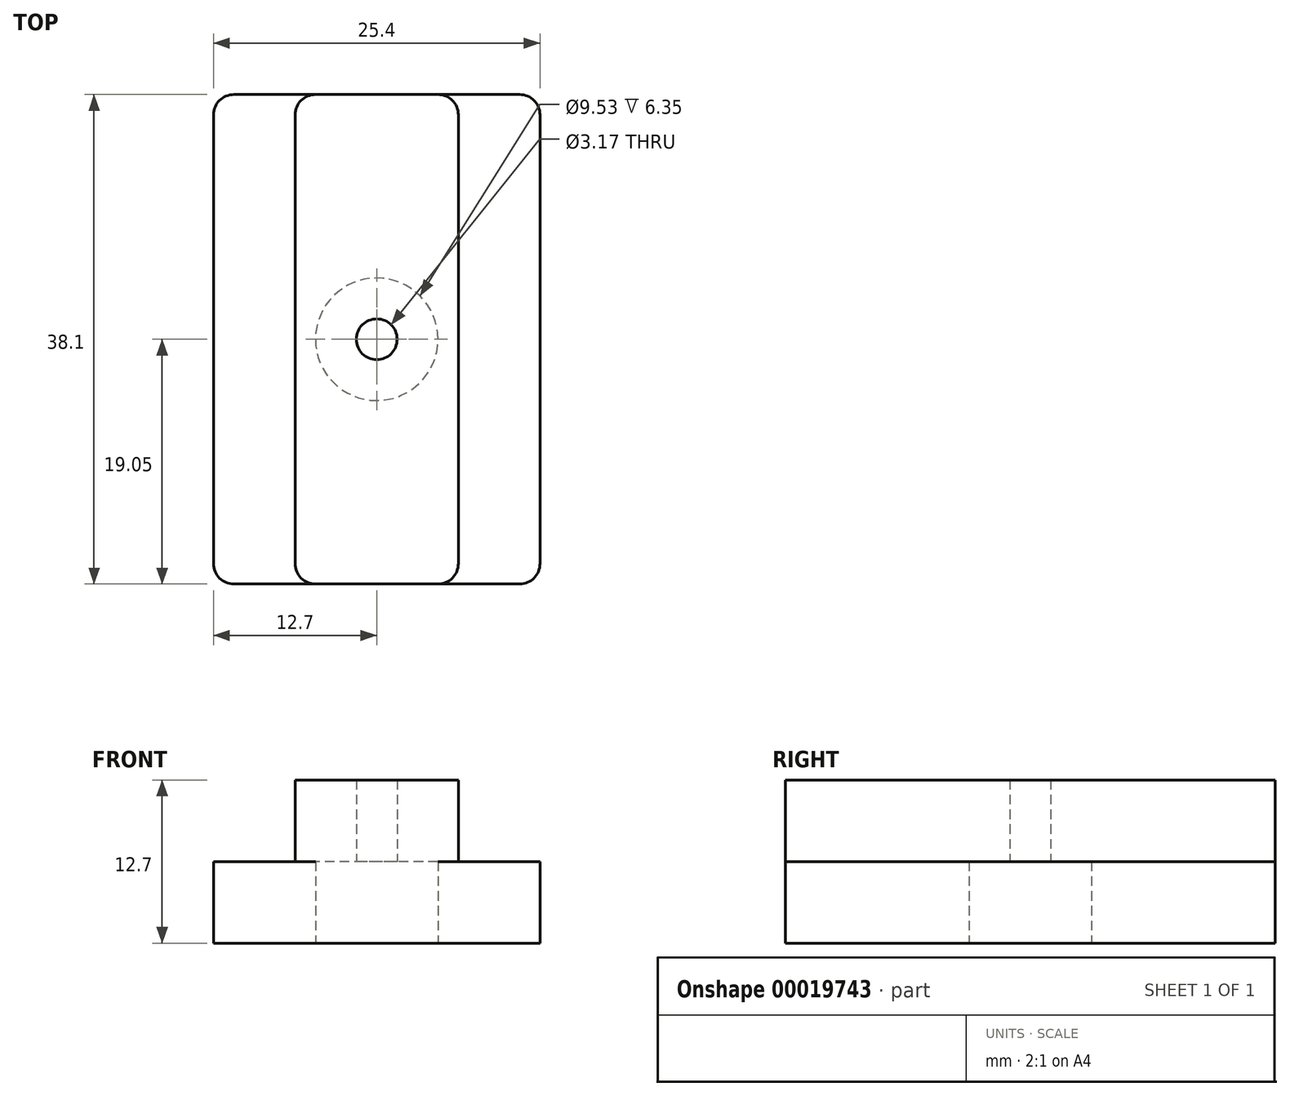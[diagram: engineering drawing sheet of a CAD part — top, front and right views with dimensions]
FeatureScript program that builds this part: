
annotation { "Feature Type Name" : "Feature", "Feature Type Description" : "" }
export const myFeature = defineFeature(function(context is Context, id is Id, definition is map)
    precondition{}
    {
        {
            var Q0;
            Q0=qCreatedBy(makeId("Top.planeOp"),FACE);
            var sketch = newSketch(context, id + "F0", { "sketchPlane" : qUnion([Q0])});
            skLineSegment(sketch, "E0.bottom", {"start": v(1.59, 0) * mm, "end": v(23.81, 0) * mm});
            skLineSegment(sketch, "E0.top", {"start": v(1.59, 38.1) * mm, "end": v(23.81, 38.1) * mm});
            skLineSegment(sketch, "E0.left", {"start": v(0, 1.59) * mm, "end": v(0, 36.51) * mm});
            skLineSegment(sketch, "E0.right", {"start": v(25.4, 1.59) * mm, "end": v(25.4, 36.51) * mm});
            skPoint(sketch, "E1.visualSharp", {"position": v(0, 38.1) * mm});
            skArc(sketch, "E1.filletArc", {"start": v(1.59, 38.1) * mm, "mid": v(0.46, 37.64) * mm, "end": v(0, 36.51) * mm});
            skPoint(sketch, "E2.visualSharp", {"position": v(25.4, 38.1) * mm});
            skArc(sketch, "E2.filletArc", {"start": v(25.4, 36.51) * mm, "mid": v(24.94, 37.64) * mm, "end": v(23.81, 38.1) * mm});
            skPoint(sketch, "E3.visualSharp", {"position": v(25.4, 0) * mm});
            skArc(sketch, "E3.filletArc", {"start": v(23.81, 0) * mm, "mid": v(24.94, 0.46) * mm, "end": v(25.4, 1.59) * mm});
            skPoint(sketch, "E4.visualSharp", {"position": v(0, 0) * mm});
            skArc(sketch, "E4.filletArc", {"start": v(0, 1.59) * mm, "mid": v(0.46, 0.46) * mm, "end": v(1.59, 0) * mm});
            skCircle(sketch, "E5", {"center": v(12.7, 19.05) * mm, "radius": 4.76 * mm});
            skSolve(sketch);
        }
        {
            var Q0;
            Q0=qSketchRegion(id+"F0",true);
            extrude(context, id + "F1", {"entities" : qUnion([Q0]), "depth" : 6.35 * mm});
        }
        {
            var Q0;
            Q0=makeQuery(id+"F1.opExtrude","CAP_FACE",FACE,{"disambiguationData":[OSD([sQuery(id+"F0.wireOp",EDGE,"E0.bottom"),sQuery(id+"F0.wireOp",EDGE,"E0.top"),sQuery(id+"F0.wireOp",EDGE,"E0.left"),sQuery(id+"F0.wireOp",EDGE,"E0.right"),sQuery(id+"F0.wireOp",EDGE,"E1.filletArc"),sQuery(id+"F0.wireOp",EDGE,"E2.filletArc"),sQuery(id+"F0.wireOp",EDGE,"E3.filletArc"),sQuery(id+"F0.wireOp",EDGE,"E4.filletArc"),sQuery(id+"F0.wireOp",EDGE,"E5")])],"isStart":false});
            var sketch = newSketch(context, id + "F2", { "sketchPlane" : qUnion([Q0])});
            skLineSegment(sketch, "E6.bottom", {"start": v(7.94, 0) * mm, "end": v(17.46, 0) * mm});
            skLineSegment(sketch, "E6.top", {"start": v(7.94, 38.1) * mm, "end": v(17.46, 38.1) * mm});
            skLineSegment(sketch, "E6.left", {"start": v(6.35, 1.59) * mm, "end": v(6.35, 36.51) * mm});
            skLineSegment(sketch, "E6.right", {"start": v(19.05, 1.59) * mm, "end": v(19.05, 36.51) * mm});
            skCircle(sketch, "E7.0", {"center": v(12.7, 19.05) * mm, "radius": 4.76 * mm, "construction": true});
            skPoint(sketch, "E8.visualSharp", {"position": v(6.35, 38.1) * mm});
            skArc(sketch, "E8.filletArc", {"start": v(7.94, 38.1) * mm, "mid": v(6.81, 37.64) * mm, "end": v(6.35, 36.51) * mm});
            skPoint(sketch, "E9.visualSharp", {"position": v(19.05, 38.1) * mm});
            skArc(sketch, "E9.filletArc", {"start": v(19.05, 36.51) * mm, "mid": v(18.59, 37.64) * mm, "end": v(17.46, 38.1) * mm});
            skPoint(sketch, "E10.visualSharp", {"position": v(19.05, 0) * mm});
            skArc(sketch, "E10.filletArc", {"start": v(17.46, 0) * mm, "mid": v(18.59, 0.46) * mm, "end": v(19.05, 1.59) * mm});
            skPoint(sketch, "E11.visualSharp", {"position": v(6.35, 0) * mm});
            skArc(sketch, "E11.filletArc", {"start": v(6.35, 1.59) * mm, "mid": v(6.81, 0.46) * mm, "end": v(7.94, 0) * mm});
            skCircle(sketch, "E12", {"center": v(12.7, 19.05) * mm, "radius": 1.59 * mm});
            skSolve(sketch);
        }
        {
            var Q0;
            Q0=qSketchRegion(id+"F2",true);
            extrude(context, id + "F3", {"entities" : qUnion([Q0]), "operationType" : NewBodyOperationType.ADD, "depth" : 6.35 * mm});
        }
    });
